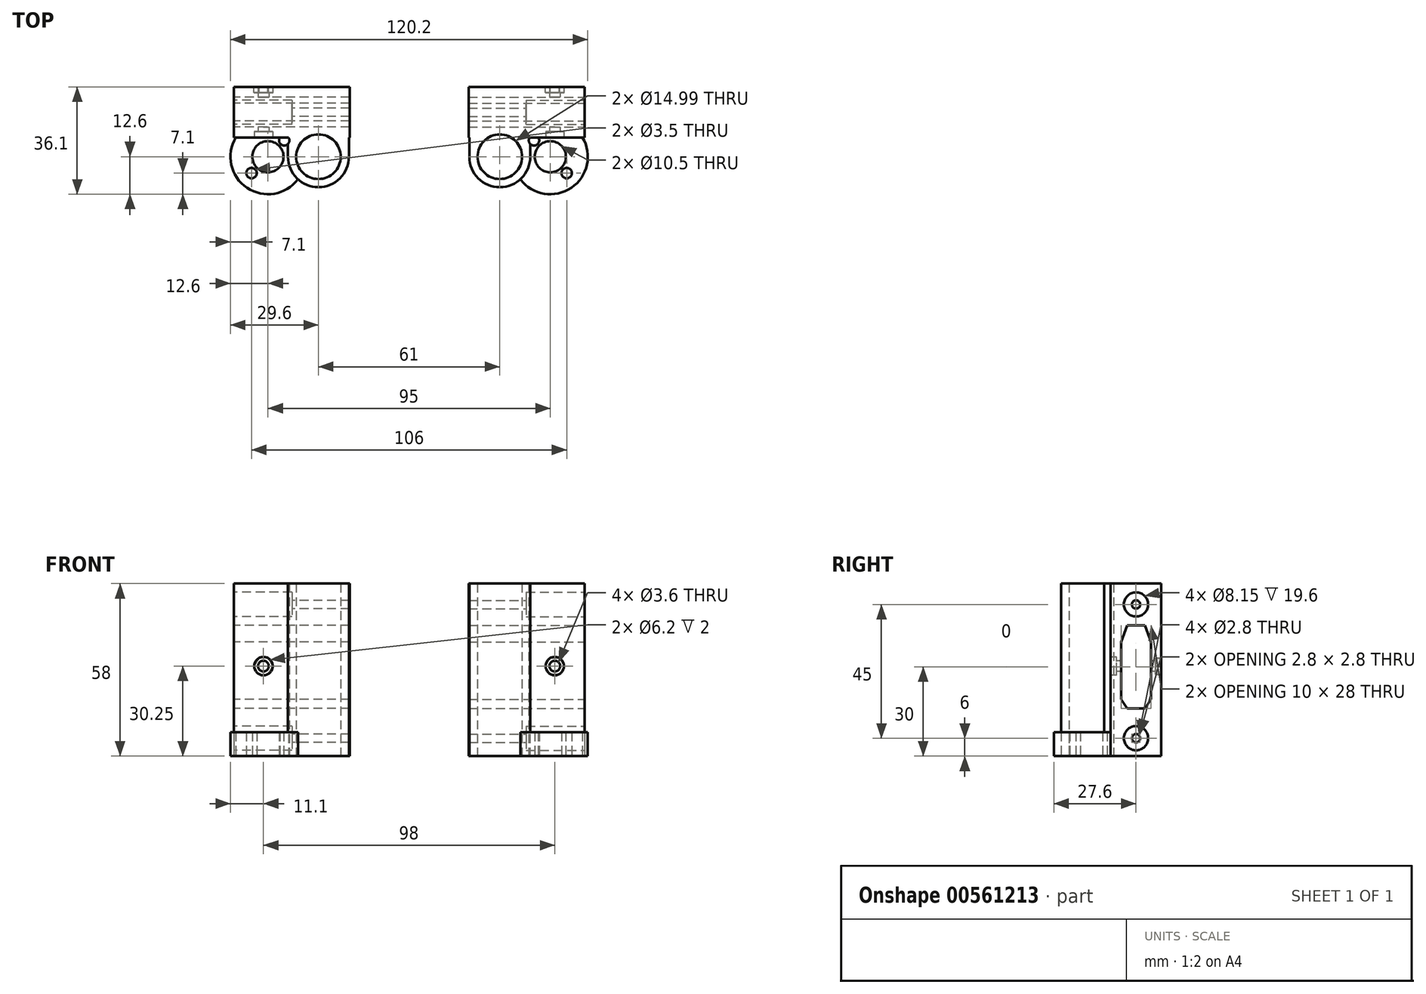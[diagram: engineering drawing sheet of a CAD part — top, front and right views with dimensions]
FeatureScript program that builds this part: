
annotation { "Feature Type Name" : "Feature", "Feature Type Description" : "" }
export const myFeature = defineFeature(function(context is Context, id is Id, definition is map)
    precondition{}
    {
        {
            var Q0;
            Q0=qCreatedBy(makeId("Front.planeOp"),FACE);
            var sketch = newSketch(context, id + "F0", { "sketchPlane" : qUnion([Q0])});
            skLineSegment(sketch, "E0.top", {"start": v(-1.75, -31) * mm, "end": v(-40.75, -31) * mm});
            skLineSegment(sketch, "E0.right", {"start": v(-40.75, 27) * mm, "end": v(-40.75, -31) * mm});
            skPoint(sketch, "E0.middle", {"position": v(0, 0) * mm});
            skLineSegment(sketch, "E1", {"start": v(27.92, -16.23) * mm, "end": v(27.98, -16.2) * mm});
            skLineSegment(sketch, "E2", {"start": v(-1.75, 27) * mm, "end": v(-1.75, -31) * mm});
            skLineSegment(sketch, "E3", {"start": v(-1.75, 27) * mm, "end": v(-40.75, 27) * mm});
            skSolve(sketch);
        }
        {
            var Q0;
            Q0=makeQuery(id+"F0.imprint","IMPRINT",FACE,{"disambiguationData":[TD([[makeQuery(id+"F0.imprint","IMPRINT",EDGE,{"derivedFrom":sQuery(id+"F0.wireOp",EDGE,"E0.top")}),-1.0]])]});
            var Q1;
            Q1=makeQuery(id+"F0.imprint","IMPRINT",FACE,{"disambiguationData":[TD([[makeQuery(id+"F0.imprint","IMPRINT",EDGE,{"derivedFrom":sQuery(id+"F0.wireOp",EDGE,"ap7tbVPz-bfE6-hNip-LwGx-kV79dPdzoOev")}),-1.0]])]});
            extrude(context, id + "F1", {"entities" : qUnion([Q0, Q1]), "depth" : 17 * mm, "offsetDistance" : 25 * mm});
        }
        {
            var Q0;
            Q0=makeQuery(id+"F1.opExtrude","SWEPT_FACE",FACE,{"disambiguationData":[OSD([sQuery(id+"F0.wireOp",EDGE,"E0.top")])]});
            var sketch = newSketch(context, id + "F2", { "sketchPlane" : qUnion([Q0])});
            skCircle(sketch, "E4", {"center": v(-12.25, 23.5) * mm, "radius": 7.5 * mm});
            skArc(sketch, "E5", {"start": v(-2, 23.5) * mm, "mid": v(-12.25, 33.75) * mm, "end": v(-22.5, 23.5) * mm});
            skLineSegment(sketch, "E6", {"start": v(-2, 23.5) * mm, "end": v(-2, 17) * mm});
            skLineSegment(sketch, "E7", {"start": v(-22.5, 23.5) * mm, "end": v(-22.5, 17) * mm});
            skCircle(sketch, "E8", {"center": v(-29.25, 23.5) * mm, "radius": 12.6 * mm});
            skCircle(sketch, "E9", {"center": v(-29.25, 23.5) * mm, "radius": 5.25 * mm});
            skLineSegment(sketch, "E10", {"start": v(-29.25, 23.5) * mm, "end": v(-34.75, 29) * mm});
            skCircle(sketch, "E11", {"center": v(-34.75, 29) * mm, "radius": 1.75 * mm});
            skLineSegment(sketch, "E12", {"start": v(-29.25, 23.5) * mm, "end": v(-23.75, 18) * mm});
            skCircle(sketch, "E13", {"center": v(-23.75, 18) * mm, "radius": 1.75 * mm});
            skSolve(sketch);
        }
        {
            var Q0;
            {var subQ0=sQuery(id+"F2.wireOp",EDGE,"E4");var subQ1=makeQuery(id+"F1.opExtrude","CAP_EDGE",EDGE,{"disambiguationData":[OSD([sQuery(id+"F0.wireOp",EDGE,"E0.top")])],"isStart":false});var subQ2=makeQuery(id+"F2.imprint","INTERSECT",VERTEX,{"disambiguationData":[OD(0.0)],"derivedFrom":[subQ1,subQ0]});Q0=makeQuery(id+"F2.imprint","IMPRINT",FACE,{"disambiguationData":[TD([[makeQuery(id+"F2.imprint","IMPRINT",EDGE,{"disambiguationData":[TD([[subQ2,-1.0]])],"derivedFrom":subQ0}),1.0]])]});}
            var Q1;
            {var subQ0=sQuery(id+"F2.wireOp",EDGE,"E13");var subQ1=makeQuery(id+"F1.opExtrude","CAP_EDGE",EDGE,{"disambiguationData":[OSD([sQuery(id+"F0.wireOp",EDGE,"E0.top")])],"isStart":false});var subQ2=makeQuery(id+"F2.imprint","INTERSECT",VERTEX,{"disambiguationData":[OD(0.0)],"derivedFrom":[subQ1,subQ0]});Q1=makeQuery(id+"F2.imprint","IMPRINT",FACE,{"disambiguationData":[TD([[makeQuery(id+"F2.imprint","IMPRINT",EDGE,{"disambiguationData":[TD([[subQ2,-1.0]])],"derivedFrom":subQ0}),1.0]])]});}
            var Q2;
            {var subQ0=sQuery(id+"F2.wireOp",EDGE,"E7");var subQ1=makeQuery(id+"F1.opExtrude","CAP_EDGE",EDGE,{"disambiguationData":[OSD([sQuery(id+"F0.wireOp",EDGE,"E0.top")])],"isStart":false});var subQ2=makeQuery(id+"F2.imprint","INTERSECT",VERTEX,{"derivedFrom":[subQ1,subQ0]});Q2=makeQuery(id+"F2.imprint","IMPRINT",FACE,{"disambiguationData":[TD([[makeQuery(id+"F2.imprint","IMPRINT",EDGE,{"disambiguationData":[TD([[subQ2,1.0]])],"derivedFrom":subQ0}),1.0]])]});}
            extrude(context, id + "F3", {"entities" : qUnion([Q0, Q1, Q2]), "operationType" : NewBodyOperationType.REMOVE, "endBound" : BoundingType.THROUGH_ALL, "oppositeDirection" : true, "depth" : 25 * mm, "offsetDistance" : 25 * mm});
        }
        {
            var Q0;
            {var subQ0=sQuery(id+"F2.wireOp",EDGE,"E8");var subQ1=sQuery(id+"F2.wireOp",EDGE,"E4");var subQ2=makeQuery(id+"F2.imprint","INTERSECT",VERTEX,{"disambiguationData":[OD(0.0)],"derivedFrom":[subQ1,subQ0]});Q0=makeQuery(id+"F2.imprint","IMPRINT",FACE,{"disambiguationData":[TD([[makeQuery(id+"F2.imprint","IMPRINT",EDGE,{"disambiguationData":[TD([[subQ2,-1.0]])],"derivedFrom":subQ1}),-1.0]])]});}
            var Q1;
            {var subQ0=sQuery(id+"F2.wireOp",EDGE,"E8");var subQ3=sQuery(id+"F2.wireOp",EDGE,"E4");var subQ9=makeQuery(id+"F2.imprint","INTERSECT",VERTEX,{"disambiguationData":[OD(0.0)],"derivedFrom":[subQ3,subQ0]});Q1=makeQuery(id+"F2.imprint","IMPRINT",FACE,{"disambiguationData":[TD([[makeQuery(id+"F2.imprint","IMPRINT",EDGE,{"disambiguationData":[TD([[subQ9,1.0]])],"derivedFrom":subQ3}),-1.0]])]});}
            var Q2;
            {var subQ0=sQuery(id+"F2.wireOp",EDGE,"E6");Q2=makeQuery(id+"F2.imprint","IMPRINT",FACE,{"disambiguationData":[TD([[makeQuery(id+"F2.imprint","IMPRINT",EDGE,{"derivedFrom":subQ0}),-1.0]])]});}
            var Q3;
            Q3=makeQuery(id+"F1.opExtrude","SWEPT_FACE",FACE,{"disambiguationData":[OSD([sQuery(id+"F0.wireOp",EDGE,"E3")])]});
            extrude(context, id + "F4", {"entities" : qUnion([Q0, Q1, Q2]), "operationType" : NewBodyOperationType.ADD, "endBound" : BoundingType.UP_TO_SURFACE, "oppositeDirection" : true, "depth" : 25 * mm, "endBoundEntityFace" : qUnion([Q3]), "offsetDistance" : 25 * mm});
        }
        {
            var Q0;
            Q0=makeQuery(id+"F2.imprint","IMPRINT",FACE,{"disambiguationData":[TD([[makeQuery(id+"F2.imprint","IMPRINT",EDGE,{"derivedFrom":sQuery(id+"F2.wireOp",EDGE,"E11")}),-1.0]])]});
            extrude(context, id + "F5", {"entities" : qUnion([Q0]), "operationType" : NewBodyOperationType.ADD, "oppositeDirection" : true, "depth" : 8 * mm, "offsetDistance" : 25 * mm});
        }
        {
            var Q0;
            Q0=makeQuery(id+"F1.opExtrude","SWEPT_FACE",FACE,{"disambiguationData":[OSD([sQuery(id+"F0.wireOp",EDGE,"E0.right")])]});
            var sketch = newSketch(context, id + "F6", { "sketchPlane" : qUnion([Q0])});
            skLineSegment(sketch, "E14", {"start": v(5.55, 13) * mm, "end": v(11.45, 13) * mm});
            skLineSegment(sketch, "E15", {"start": v(11.45, 13) * mm, "end": v(13.5, 7.38) * mm});
            skLineSegment(sketch, "E16", {"start": v(13.5, 7.38) * mm, "end": v(13.5, -11.93) * mm});
            skLineSegment(sketch, "E17", {"start": v(13.5, -11.93) * mm, "end": v(11.45, -15) * mm});
            skLineSegment(sketch, "E18", {"start": v(11.45, -15) * mm, "end": v(5.55, -15) * mm});
            skLineSegment(sketch, "E19", {"start": v(5.55, -15) * mm, "end": v(3.5, -11.93) * mm});
            skLineSegment(sketch, "E20", {"start": v(3.5, -11.93) * mm, "end": v(3.5, 7.38) * mm});
            skLineSegment(sketch, "E21", {"start": v(3.5, 7.38) * mm, "end": v(5.55, 13) * mm});
            skCircle(sketch, "E22", {"center": v(8.5, 20) * mm, "radius": 4.08 * mm});
            skPoint(sketch, "E22.centerSnap0", {"position": v(8.5, 27) * mm});
            skCircle(sketch, "E23", {"center": v(8.5, -25) * mm, "radius": 4.08 * mm});
            skPoint(sketch, "E23.centerSnap0", {"position": v(8.5, -31) * mm});
            skSolve(sketch);
        }
        {
            var Q0;
            Q0=makeQuery(id+"F6.imprint","IMPRINT",FACE,{"disambiguationData":[TD([[makeQuery(id+"F6.imprint","IMPRINT",EDGE,{"derivedFrom":sQuery(id+"F6.wireOp",EDGE,"E14")}),-1.0]])]});
            extrude(context, id + "F7", {"entities" : qUnion([Q0]), "operationType" : NewBodyOperationType.REMOVE, "endBound" : BoundingType.THROUGH_ALL, "oppositeDirection" : true, "depth" : 25 * mm, "offsetDistance" : 25 * mm});
        }
        {
            var Q0;
            Q0=makeQuery(id+"F6.imprint","IMPRINT",FACE,{"disambiguationData":[TD([[makeQuery(id+"F6.imprint","IMPRINT",EDGE,{"derivedFrom":sQuery(id+"F6.wireOp",EDGE,"E22")}),1.0]])]});
            var Q1;
            Q1=makeQuery(id+"F6.imprint","IMPRINT",FACE,{"disambiguationData":[TD([[makeQuery(id+"F6.imprint","IMPRINT",EDGE,{"derivedFrom":sQuery(id+"F6.wireOp",EDGE,"E23")}),1.0]])]});
            extrude(context, id + "F8", {"entities" : qUnion([Q0, Q1]), "operationType" : NewBodyOperationType.REMOVE, "oppositeDirection" : true, "depth" : 19.6 * mm, "offsetDistance" : 25 * mm});
        }
        {
            var Q0;
            Q0=makeQuery(id+"F8.boolean.opBoolean","COPY",FACE,{"derivedFrom":makeQuery(id+"F8.opExtrude","CAP_FACE",FACE,{"disambiguationData":[OSD([sQuery(id+"F6.wireOp",EDGE,"E22")])],"isStart":false})});
            var sketch = newSketch(context, id + "F9", { "sketchPlane" : qUnion([Q0])});
            skCircle(sketch, "E24", {"center": v(8.5, 20) * mm, "radius": 1.4 * mm});
            skSolve(sketch);
        }
        {
            var Q0;
            Q0=makeQuery(id+"F8.boolean.opBoolean","COPY",FACE,{"derivedFrom":makeQuery(id+"F8.opExtrude","CAP_FACE",FACE,{"disambiguationData":[OSD([sQuery(id+"F6.wireOp",EDGE,"E23")])],"isStart":false})});
            var sketch = newSketch(context, id + "F10", { "sketchPlane" : qUnion([Q0])});
            skCircle(sketch, "E25", {"center": v(8.5, -25) * mm, "radius": 1.4 * mm});
            skSolve(sketch);
        }
        {
            var Q0;
            Q0=makeQuery(id+"F10.imprint","IMPRINT",FACE,{"disambiguationData":[TD([[makeQuery(id+"F10.imprint","IMPRINT",EDGE,{"derivedFrom":sQuery(id+"F10.wireOp",EDGE,"E25")}),1.0]])]});
            var Q1;
            Q1=makeQuery(id+"F9.imprint","IMPRINT",FACE,{"disambiguationData":[TD([[makeQuery(id+"F9.imprint","IMPRINT",EDGE,{"derivedFrom":sQuery(id+"F9.wireOp",EDGE,"E24")}),1.0]])]});
            extrude(context, id + "F11", {"entities" : qUnion([Q0, Q1]), "operationType" : NewBodyOperationType.REMOVE, "endBound" : BoundingType.THROUGH_ALL, "oppositeDirection" : true, "depth" : 25 * mm, "offsetDistance" : 25 * mm});
        }
        {
            var Q0;
            Q0=makeQuery(id+"F7.boolean.opBoolean","COPY",FACE,{"derivedFrom":makeQuery(id+"F7.opExtrude","SWEPT_FACE",FACE,{"disambiguationData":[OSD([sQuery(id+"F6.wireOp",EDGE,"E20")])]})});
            var sketch = newSketch(context, id + "F12", { "sketchPlane" : qUnion([Q0])});
            skCircle(sketch, "E26", {"center": v(-30.75, -0.75) * mm, "radius": 1.8 * mm});
            skSolve(sketch);
        }
        {
            var Q0;
            Q0=makeQuery(id+"F12.imprint","IMPRINT",FACE,{"disambiguationData":[TD([[makeQuery(id+"F12.imprint","IMPRINT",EDGE,{"derivedFrom":sQuery(id+"F12.wireOp",EDGE,"E26")}),1.0]])]});
            var Q1;
            Q1=sQuery(id+"F12.wireOp",EDGE,"E26");
            extrude(context, id + "F13", {"entities" : qUnion([Q0]), "operationType" : NewBodyOperationType.REMOVE, "surfaceEntities" : qUnion([Q1]), "endBound" : BoundingType.THROUGH_ALL, "oppositeDirection" : true, "depth" : 25 * mm, "offsetDistance" : 25 * mm, "hasSecondDirection" : true, "secondDirectionBound" : SecondDirectionBoundingType.THROUGH_ALL, "secondDirectionOppositeDirection" : false, "secondDirectionDepth" : 25 * mm});
        }
        {
            var Q0;
            {var subQ0=sQuery(id+"F0.wireOp",EDGE,"E0.top");var subQ1=sQuery(id+"F0.wireOp",EDGE,"E3");var subQ2=sQuery(id+"F0.wireOp",EDGE,"E0.right");Q0=makeQuery(id+"F3.boolean.opBoolean","SPLIT",FACE,{"disambiguationData":[TD([makeQuery(id+"F1.opExtrude","SWEPT_FACE",FACE,{"disambiguationData":[OSD([subQ0])]}),makeQuery(id+"F1.opExtrude","SWEPT_FACE",FACE,{"disambiguationData":[OSD([subQ2])]}),makeQuery(id+"F1.opExtrude","SWEPT_FACE",FACE,{"disambiguationData":[OSD([subQ1])]}),makeQuery(id+"F3.opExtrude","SWEPT_FACE",FACE,{"disambiguationData":[OSD([sQuery(id+"F2.wireOp",EDGE,"E13")])]})])],"derivedFrom":makeQuery(id+"F1.opExtrude","CAP_FACE",FACE,{"disambiguationData":[OSD([subQ0,subQ2,sQuery(id+"F0.wireOp",EDGE,"E2"),subQ1])],"isStart":false})});}
            var sketch = newSketch(context, id + "F14", { "sketchPlane" : qUnion([Q0])});
            skCircle(sketch, "E27", {"center": v(-30.75, -0.75) * mm, "radius": 3.1 * mm});
            skSolve(sketch);
        }
        {
            var Q0;
            Q0=makeQuery(id+"F14.imprint","IMPRINT",FACE,{"disambiguationData":[TD([[makeQuery(id+"F14.imprint","IMPRINT",EDGE,{"derivedFrom":sQuery(id+"F14.wireOp",EDGE,"E27")}),1.0]])]});
            extrude(context, id + "F15", {"entities" : qUnion([Q0]), "operationType" : NewBodyOperationType.REMOVE, "oppositeDirection" : true, "depth" : 2 * mm, "offsetDistance" : 25 * mm});
        }
        {
            var Q0;
            Q0=makeQuery(id+"F1.opExtrude","CAP_FACE",FACE,{"disambiguationData":[OSD([sQuery(id+"F0.wireOp",EDGE,"E0.top"),sQuery(id+"F0.wireOp",EDGE,"E0.right"),sQuery(id+"F0.wireOp",EDGE,"E2"),sQuery(id+"F0.wireOp",EDGE,"E3")])],"isStart":true});
            var sketch = newSketch(context, id + "F16", { "sketchPlane" : qUnion([Q0])});
            skCircle(sketch, "E28.cCircle", {"center": v(30.75, -0.75) * mm, "radius": 2.77 * mm, "construction": true});
            skLineSegment(sketch, "E28.0", {"start": v(32.26, 2.07) * mm, "end": v(33.95, -0.64) * mm});
            skLineSegment(sketch, "E28.1", {"start": v(33.95, -0.64) * mm, "end": v(32.44, -3.47) * mm});
            skLineSegment(sketch, "E28.2", {"start": v(32.44, -3.47) * mm, "end": v(29.24, -3.57) * mm});
            skLineSegment(sketch, "E28.3", {"start": v(29.24, -3.57) * mm, "end": v(27.55, -0.86) * mm});
            skLineSegment(sketch, "E28.4", {"start": v(27.55, -0.86) * mm, "end": v(29.06, 1.97) * mm});
            skLineSegment(sketch, "E28.5", {"start": v(29.06, 1.97) * mm, "end": v(32.26, 2.07) * mm});
            skPoint(sketch, "E28.0.midPoint", {"position": v(33.1, 0.71) * mm});
            skSolve(sketch);
        }
        {
            var Q0;
            Q0=makeQuery(id+"F16.imprint","IMPRINT",FACE,{"disambiguationData":[TD([[makeQuery(id+"F16.imprint","IMPRINT",EDGE,{"derivedFrom":sQuery(id+"F16.wireOp",EDGE,"E28.0")}),-1.0]])]});
            extrude(context, id + "F17", {"entities" : qUnion([Q0]), "operationType" : NewBodyOperationType.REMOVE, "oppositeDirection" : true, "depth" : 2 * mm, "offsetDistance" : 25 * mm});
        }
        {
            var Q0;
            Q0=makeQuery(id+"F1.opExtrude","SWEPT_BODY",BODY,{"disambiguationData":[OSD([sQuery(id+"F0.wireOp",EDGE,"E0.top"),sQuery(id+"F0.wireOp",EDGE,"E0.right"),sQuery(id+"F0.wireOp",EDGE,"E2"),sQuery(id+"F0.wireOp",EDGE,"E3")])]});
            var Q1;
            Q1=makeQuery(id+"F1.opExtrude","SWEPT_FACE",FACE,{"disambiguationData":[OSD([sQuery(id+"F0.wireOp",EDGE,"E2")])]});
            mirror(context, id + "F18", {"entities" : qUnion([Q0]), "mirrorPlane" : qUnion([Q1])});
        }
        {
            var Q0;
            Q0=makeQuery(id+"F18.opPattern","COPY",BODY,{"derivedFrom":makeQuery(id+"F1.opExtrude","SWEPT_BODY",BODY,{"disambiguationData":[OSD([sQuery(id+"F0.wireOp",EDGE,"E0.top"),sQuery(id+"F0.wireOp",EDGE,"E0.right"),sQuery(id+"F0.wireOp",EDGE,"E2"),sQuery(id+"F0.wireOp",EDGE,"E3")])]}),"instanceName":"1"});
            transform(context, id + "F19", {"entities" : qUnion([Q0]), "transformType" : TransformType.TRANSLATION_3D, "dx" : 40 * mm, "dy" : 0 * mm, "dz" : 0 * mm, "makeCopy" : false});
        }
    });
